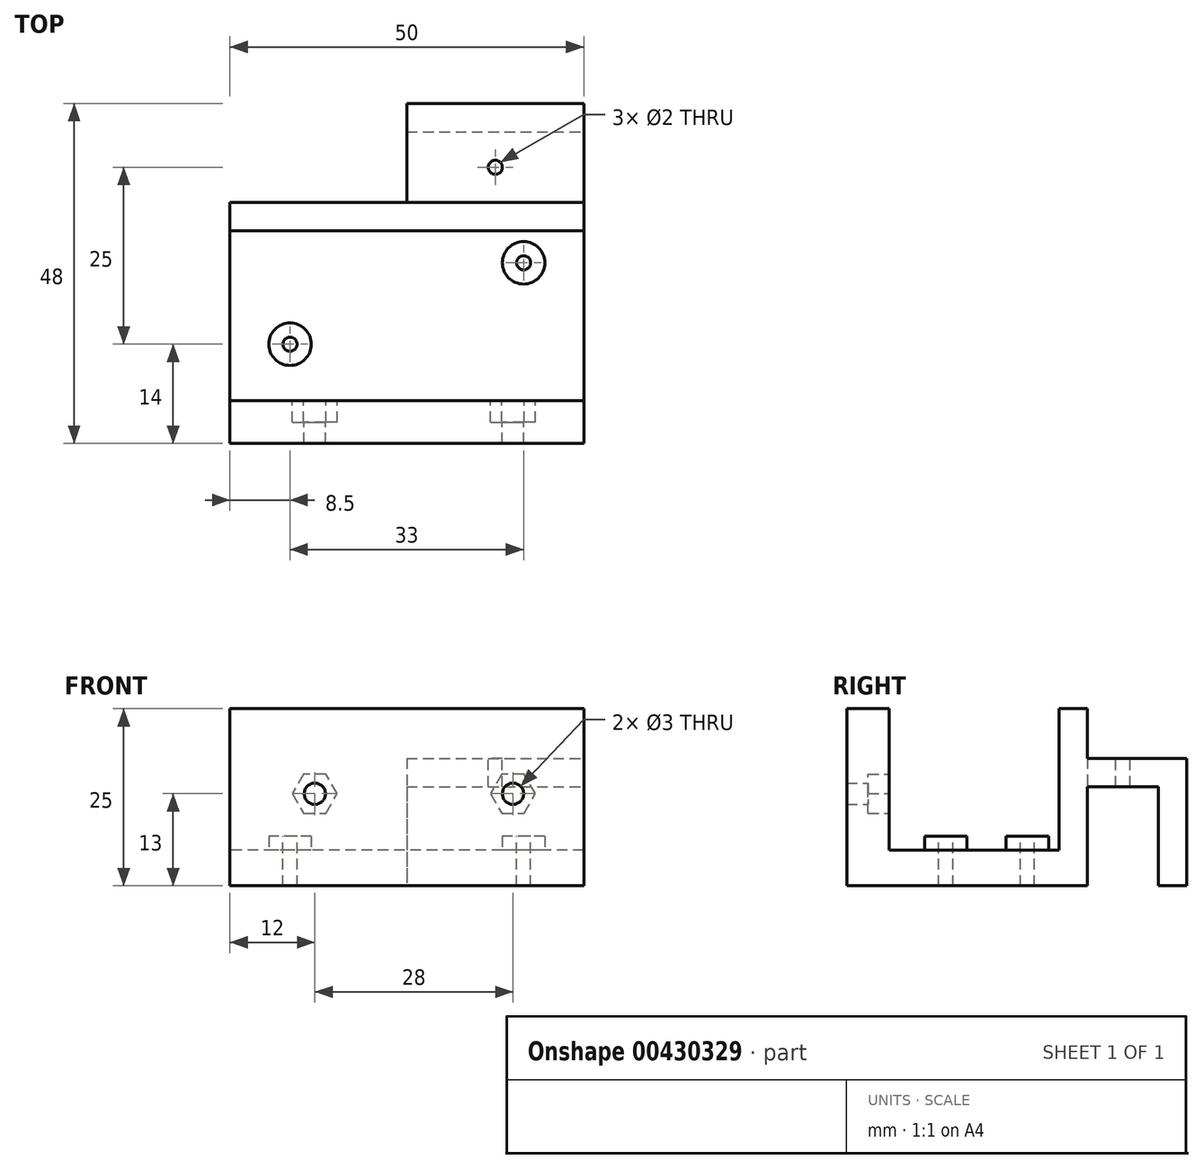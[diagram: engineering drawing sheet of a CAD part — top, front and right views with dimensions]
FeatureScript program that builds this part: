
annotation { "Feature Type Name" : "Feature", "Feature Type Description" : "" }
export const myFeature = defineFeature(function(context is Context, id is Id, definition is map)
    precondition{}
    {
        {
            var Q0;
            Q0=qCreatedBy(makeId("Right.planeOp"),FACE);
            var sketch = newSketch(context, id + "F0", { "sketchPlane" : qUnion([Q0])});
            skLineSegment(sketch, "E0.bottom", {"start": v(6, 25) * mm, "end": v(0, 25) * mm});
            skLineSegment(sketch, "E0.left", {"start": v(6, 25) * mm, "end": v(6, 5) * mm});
            skLineSegment(sketch, "E0.right", {"start": v(0, 25) * mm, "end": v(0, 0) * mm});
            skLineSegment(sketch, "E1.bottom", {"start": v(0, 0) * mm, "end": v(34, 0) * mm});
            skLineSegment(sketch, "E1.top", {"start": v(6, 5) * mm, "end": v(30, 5) * mm});
            skLineSegment(sketch, "E2.bottom", {"start": v(30, 25) * mm, "end": v(34, 25) * mm});
            skLineSegment(sketch, "E2.left", {"start": v(30, 25) * mm, "end": v(30, 5) * mm});
            skLineSegment(sketch, "E2.right", {"start": v(34, 25) * mm, "end": v(34, 0) * mm});
            skSolve(sketch);
        }
        {
            var Q0;
            Q0=qSketchRegion(id+"F0",true);
            extrude(context, id + "F1", {"entities" : qUnion([Q0]), "depth" : 50 * mm, "offsetDistance" : 25 * mm});
        }
        {
            var Q0;
            Q0=makeQuery(id+"F1.opExtrude","SWEPT_FACE",FACE,{"disambiguationData":[OSD([sQuery(id+"F0.wireOp",EDGE,"E0.left")])]});
            var sketch = newSketch(context, id + "F2", { "sketchPlane" : qUnion([Q0])});
            skCircle(sketch, "E3", {"center": v(-40, 13) * mm, "radius": 1.5 * mm});
            skCircle(sketch, "E4", {"center": v(-12, 13) * mm, "radius": 1.5 * mm});
            skCircle(sketch, "E5.cCircle", {"center": v(-40, 13) * mm, "radius": 3.18 * mm, "construction": true});
            skLineSegment(sketch, "E5.0", {"start": v(-43.18, 13) * mm, "end": v(-41.59, 15.75) * mm});
            skLineSegment(sketch, "E5.1", {"start": v(-41.59, 15.75) * mm, "end": v(-38.41, 15.75) * mm});
            skLineSegment(sketch, "E5.2", {"start": v(-38.41, 15.75) * mm, "end": v(-36.82, 13) * mm});
            skLineSegment(sketch, "E5.3", {"start": v(-36.82, 13) * mm, "end": v(-38.41, 10.25) * mm});
            skLineSegment(sketch, "E5.4", {"start": v(-38.41, 10.25) * mm, "end": v(-41.59, 10.25) * mm});
            skLineSegment(sketch, "E5.5", {"start": v(-41.59, 10.25) * mm, "end": v(-43.18, 13) * mm});
            skCircle(sketch, "E6.cCircle", {"center": v(-12, 13) * mm, "radius": 3.18 * mm, "construction": true});
            skLineSegment(sketch, "E6.0", {"start": v(-15.18, 13) * mm, "end": v(-13.59, 15.75) * mm});
            skLineSegment(sketch, "E6.1", {"start": v(-13.59, 15.75) * mm, "end": v(-10.41, 15.75) * mm});
            skLineSegment(sketch, "E6.2", {"start": v(-10.41, 15.75) * mm, "end": v(-8.82, 13) * mm});
            skLineSegment(sketch, "E6.3", {"start": v(-8.82, 13) * mm, "end": v(-10.41, 10.25) * mm});
            skLineSegment(sketch, "E6.4", {"start": v(-10.41, 10.25) * mm, "end": v(-13.59, 10.25) * mm});
            skLineSegment(sketch, "E6.5", {"start": v(-13.59, 10.25) * mm, "end": v(-15.18, 13) * mm});
            skSolve(sketch);
        }
        {
            var Q0;
            Q0=makeQuery(id+"F2.imprint","IMPRINT",FACE,{"disambiguationData":[TD([[makeQuery(id+"F2.imprint","IMPRINT",EDGE,{"derivedFrom":sQuery(id+"F2.wireOp",EDGE,"E3")}),1.0]])]});
            var Q1;
            Q1=makeQuery(id+"F2.imprint","IMPRINT",FACE,{"disambiguationData":[TD([[makeQuery(id+"F2.imprint","IMPRINT",EDGE,{"derivedFrom":sQuery(id+"F2.wireOp",EDGE,"E4")}),1.0]])]});
            extrude(context, id + "F3", {"entities" : qUnion([Q0, Q1]), "operationType" : NewBodyOperationType.REMOVE, "endBound" : BoundingType.THROUGH_ALL, "oppositeDirection" : true, "depth" : 25 * mm, "offsetDistance" : 25 * mm});
        }
        {
            var Q0;
            Q0=makeQuery(id+"F2.imprint","IMPRINT",FACE,{"disambiguationData":[TD([[makeQuery(id+"F2.imprint","IMPRINT",EDGE,{"derivedFrom":sQuery(id+"F2.wireOp",EDGE,"E3")}),-1.0]])]});
            var Q1;
            Q1=makeQuery(id+"F2.imprint","IMPRINT",FACE,{"disambiguationData":[TD([[makeQuery(id+"F2.imprint","IMPRINT",EDGE,{"derivedFrom":sQuery(id+"F2.wireOp",EDGE,"E4")}),-1.0]])]});
            extrude(context, id + "F4", {"entities" : qUnion([Q0, Q1]), "operationType" : NewBodyOperationType.REMOVE, "endBound" : BoundingType.UP_TO_NEXT, "oppositeDirection" : true, "depth" : 4 * mm, "hasOffset" : true, "offsetDistance" : 3 * mm});
        }
        {
            var Q0;
            Q0=makeQuery(id+"F1.opExtrude","SWEPT_FACE",FACE,{"disambiguationData":[OSD([sQuery(id+"F0.wireOp",EDGE,"E1.top")])]});
            var sketch = newSketch(context, id + "F5", { "sketchPlane" : qUnion([Q0])});
            skCircle(sketch, "E7", {"center": v(8.5, 14) * mm, "radius": 1 * mm});
            skCircle(sketch, "E8", {"center": v(8.5, 14) * mm, "radius": 3 * mm});
            skCircle(sketch, "E9", {"center": v(41.5, 25.5) * mm, "radius": 1 * mm});
            skCircle(sketch, "E10", {"center": v(41.5, 25.5) * mm, "radius": 3 * mm});
            skLineSegment(sketch, "E11", {"start": v(8.5, 14) * mm, "end": v(0, 14) * mm, "construction": true});
            skLineSegment(sketch, "E12", {"start": v(50, 25.5) * mm, "end": v(41.5, 25.5) * mm, "construction": true});
            skSolve(sketch);
        }
        {
            var Q0;
            Q0=makeQuery(id+"F5.imprint","IMPRINT",FACE,{"disambiguationData":[TD([[makeQuery(id+"F5.imprint","IMPRINT",EDGE,{"derivedFrom":sQuery(id+"F5.wireOp",EDGE,"E7")}),1.0]])]});
            var Q1;
            Q1=makeQuery(id+"F5.imprint","IMPRINT",FACE,{"disambiguationData":[TD([[makeQuery(id+"F5.imprint","IMPRINT",EDGE,{"derivedFrom":sQuery(id+"F5.wireOp",EDGE,"E9")}),1.0]])]});
            extrude(context, id + "F6", {"entities" : qUnion([Q0, Q1]), "operationType" : NewBodyOperationType.REMOVE, "endBound" : BoundingType.THROUGH_ALL, "oppositeDirection" : true, "depth" : 25 * mm, "offsetDistance" : 25 * mm});
        }
        {
            var Q0;
            Q0=makeQuery(id+"F5.imprint","IMPRINT",FACE,{"disambiguationData":[TD([[makeQuery(id+"F5.imprint","IMPRINT",EDGE,{"derivedFrom":sQuery(id+"F5.wireOp",EDGE,"E7")}),-1.0]])]});
            var Q1;
            Q1=makeQuery(id+"F5.imprint","IMPRINT",FACE,{"disambiguationData":[TD([[makeQuery(id+"F5.imprint","IMPRINT",EDGE,{"derivedFrom":sQuery(id+"F5.wireOp",EDGE,"E9")}),-1.0]])]});
            extrude(context, id + "F7", {"entities" : qUnion([Q0, Q1]), "operationType" : NewBodyOperationType.ADD, "depth" : 2 * mm, "offsetDistance" : 25 * mm});
        }
        {
            var Q0;
            Q0=makeQuery(id+"F1.opExtrude","CAP_FACE",FACE,{"disambiguationData":[OSD([sQuery(id+"F0.wireOp",EDGE,"E0.bottom"),sQuery(id+"F0.wireOp",EDGE,"E0.left"),sQuery(id+"F0.wireOp",EDGE,"E0.right"),sQuery(id+"F0.wireOp",EDGE,"E1.bottom"),sQuery(id+"F0.wireOp",EDGE,"E1.top"),sQuery(id+"F0.wireOp",EDGE,"E2.bottom"),sQuery(id+"F0.wireOp",EDGE,"E2.left"),sQuery(id+"F0.wireOp",EDGE,"E2.right")])],"isStart":false});
            var sketch = newSketch(context, id + "F8", { "sketchPlane" : qUnion([Q0])});
            skLineSegment(sketch, "E13.bottom", {"start": v(34, 18) * mm, "end": v(48, 18) * mm});
            skLineSegment(sketch, "E13.top", {"start": v(34, 14) * mm, "end": v(44, 14) * mm});
            skLineSegment(sketch, "E13.left", {"start": v(34, 18) * mm, "end": v(34, 14) * mm});
            skLineSegment(sketch, "E14.top", {"start": v(44, 0) * mm, "end": v(48, 0) * mm});
            skLineSegment(sketch, "E14.left", {"start": v(44, 14) * mm, "end": v(44, 0) * mm});
            skLineSegment(sketch, "E14.right", {"start": v(48, 18) * mm, "end": v(48, 0) * mm});
            skSolve(sketch);
        }
        {
            var Q0;
            Q0=qSketchRegion(id+"F8",true);
            extrude(context, id + "F9", {"entities" : qUnion([Q0]), "operationType" : NewBodyOperationType.ADD, "oppositeDirection" : true, "depth" : 25 * mm, "offsetDistance" : 25 * mm});
        }
        {
            var Q0;
            Q0=makeQuery(id+"F9.opExtrude","SWEPT_FACE",FACE,{"disambiguationData":[OSD([sQuery(id+"F8.wireOp",EDGE,"E13.bottom")])]});
            var sketch = newSketch(context, id + "F10", { "sketchPlane" : qUnion([Q0])});
            skLineSegment(sketch, "E15", {"start": v(37.5, 44) * mm, "end": v(37.5, 34) * mm, "construction": true});
            skCircle(sketch, "E16", {"center": v(37.5, 39) * mm, "radius": 1 * mm});
            skSolve(sketch);
        }
        {
            var Q0;
            Q0=qSketchRegion(id+"F10",true);
            extrude(context, id + "F11", {"entities" : qUnion([Q0]), "operationType" : NewBodyOperationType.REMOVE, "endBound" : BoundingType.THROUGH_ALL, "oppositeDirection" : true, "depth" : 25 * mm, "offsetDistance" : 25 * mm});
        }
    });
